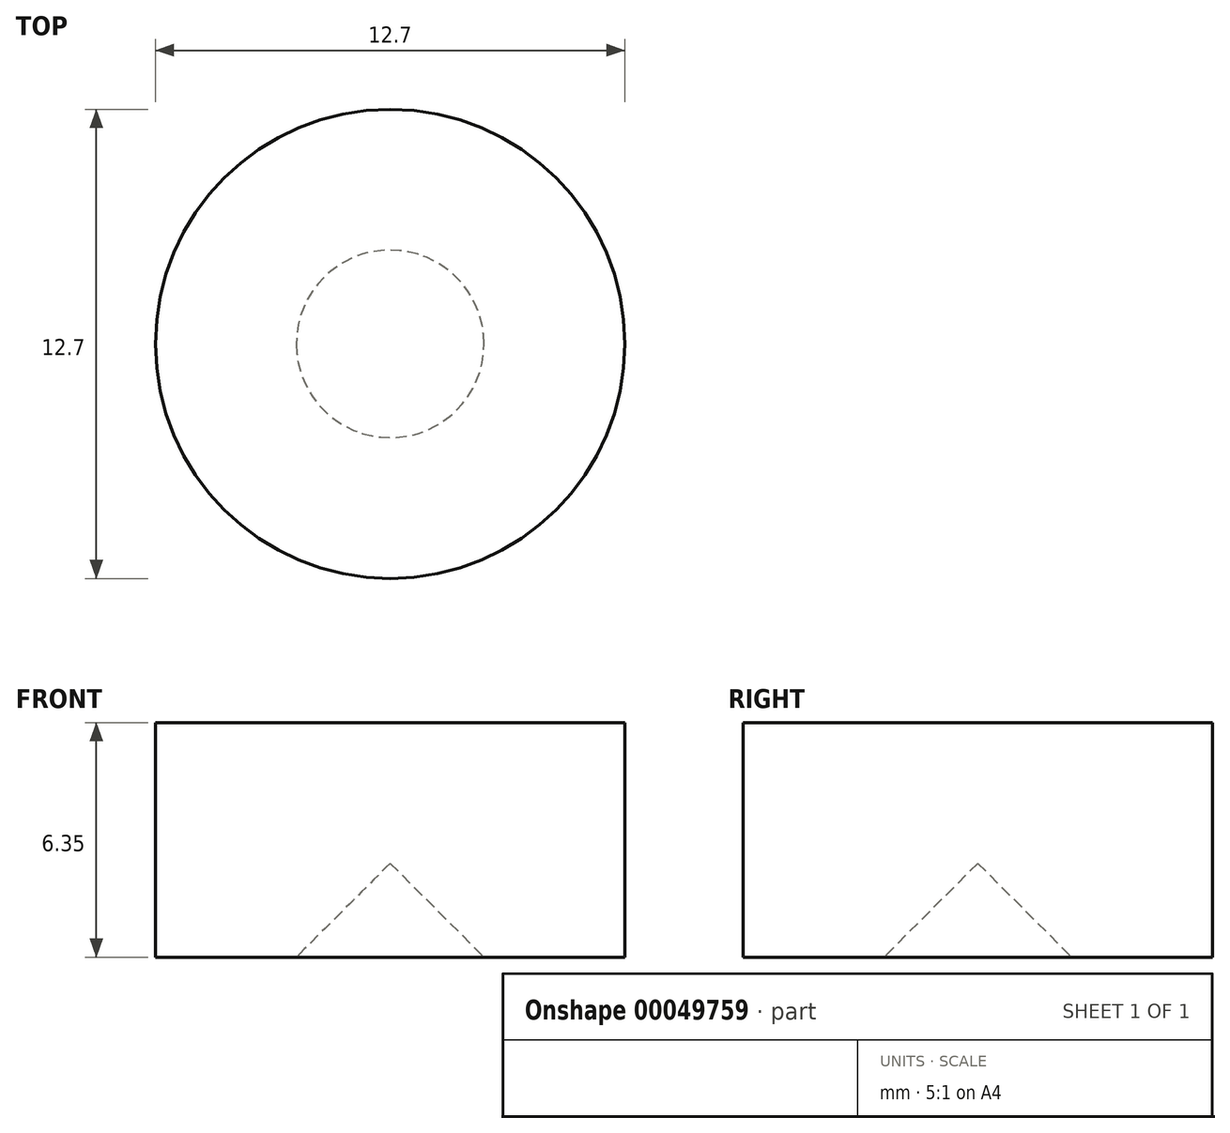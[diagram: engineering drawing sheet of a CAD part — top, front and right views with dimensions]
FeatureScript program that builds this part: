
annotation { "Feature Type Name" : "Feature", "Feature Type Description" : "" }
export const myFeature = defineFeature(function(context is Context, id is Id, definition is map)
    precondition{}
    {
        {
            var Q0;
            Q0=qCreatedBy(makeId("Top.planeOp"),FACE);
            var sketch = newSketch(context, id + "F0", { "sketchPlane" : qUnion([Q0])});
            skCircle(sketch, "E0", {"center": v(0, 0) * mm, "radius": 6.35 * mm});
            skSolve(sketch);
        }
        {
            var Q0;
            Q0 = qSketchRegion(id + "F0", true);
            extrude(context, id + "F1", {"entities" : qUnion([Q0]), "depth" : 6.35 * mm});
        }
        {
            var Q0;
            Q0=qCreatedBy(makeId("Top.planeOp"),FACE);
            var sketch = newSketch(context, id + "F2", { "sketchPlane" : qUnion([Q0])});
            skCircle(sketch, "E1", {"center": v(0, 0) * mm, "radius": 2.54 * mm});
            skSolve(sketch);
        }
        {
            var Q0;
            Q0=makeQuery(id+"F2.imprint","IMPRINT",FACE,{"disambiguationData":[TD([[makeQuery(id+"F2.imprint","IMPRINT",EDGE,{"derivedFrom":sQuery(id+"F2.wireOp",EDGE,"E1")}),1.0]])]});
            cPlane(context, id + "F3", {"entities" : qUnion([Q0]), "cplaneType" : CPlaneType.OFFSET, "offset" : 2.54 * mm, "width" : 152.4 * mm, "height" : 152.4 * mm});
        }
        {
            var Q0;
            Q0=qCreatedBy(id+"F3.planeOp",FACE);
            var sketch = newSketch(context, id + "F4", { "sketchPlane" : qUnion([Q0])});
            skPoint(sketch, "E2", {"position": v(0, 0) * mm});
            skSolve(sketch);
        }
        {
            var Q0;
            Q0=sQuery(id+"F4.wireOp",VERTEX,"E2");
            var Q1;
            Q1=makeQuery(id+"F2.imprint","IMPRINT",FACE,{"disambiguationData":[TD([[makeQuery(id+"F2.imprint","IMPRINT",EDGE,{"derivedFrom":sQuery(id+"F2.wireOp",EDGE,"E1")}),1.0]])]});
            loft(context, id + "F5", {"operationType" : NewBodyOperationType.REMOVE, "sheetProfilesArray" : [{ "sheetProfileEntities" : qUnion([Q0]) }, { "sheetProfileEntities" : qUnion([Q1]) }]});
        }
    });
